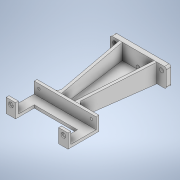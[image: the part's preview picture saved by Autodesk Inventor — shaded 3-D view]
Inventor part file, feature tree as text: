
AUTODESK INVENTOR PART (.ipt)
format: ipt  version: 2022 (Build 260153000, 153)  size: 266,240 bytes
history: native  units: mm
features: sketch x13, extrude x10, plane x1, loft x1, fillet x1, chamfer x1, other x1
ambient origin geometry x8: Origin, YZ Plane, XZ Plane, XY Plane, X Axis, Y Axis, Z Axis, Center Point
bodies: Solid1 (feature_tree)
feature tree (28):
  extrude  "Extrusion1"  Depth=3.0mm
  sketch  "Sketch2"  dims[d16=66.05mm d18=15.0mm]
  plane  "Work Plane1"
  loft  "Loft1"
  extrude  "Extrusion2"  Depth=3.0mm
  extrude  "Extrusion3"  Depth=3.0mm TaperAngle=0.0deg
  extrude  "Extrusion4"  Depth=7.5mm
  extrude  "Extrusion5"  Depth=56.05mm
  extrude  "Extrusion8"  Depth=2.5mm
  extrude  "Extrusion9"  TaperAngle=0.0deg  [1 undecoded]
  extrude  "Extrusion10"  Depth=5.0mm
  extrude  "Extrusion13"  Depth=5.0mm
  fillet  "Fillet1"  Radius=5.0mm
  chamfer  "Chamfer1"  Distance=1.0mm
  extrude  "Extrusion15"  Depth=20.0mm
  sketch  "Sketch1"  dims[d2=5.0mm d3=0.0mm d6=3.0mm d11=80.0mm]
  sketch  "Sketch3"  dims[d19=3.0mm d20=0.0mm d22=3.0mm]
  sketch  "Sketch4"  dims[d23=27.0mm d24=0.0mm d25=3.0mm d26=0.0mm]
  sketch  "Sketch5"  dims[d27=7.5mm d28=7.5mm]
  sketch  "Sketch6"  dims[d29=56.05mm d30=28.025mm]
  sketch  "Sketch7"  dims[d31=2.5mm d32=2.5mm]
  sketch  "Sketch10"  dims[d33=35.0mm d34=0.0mm d57=0.0mm d58=90.0deg]
  sketch  "Sketch11"  dims[d61=5.0mm d62=5.0mm]
  other  "Edges1"
  sketch  "Sketch12"  dims[d63=1.0mm d64=0.0mm d65=5.0mm d66=5.0mm d67=1.0mm d68=0.0mm]
  sketch  "Sketch15"  dims[d69=20.0mm d70=40.0mm]
  sketch  "Sketch16"  dims[d71=20.0mm]
  sketch  "Sketch17"  dims[d72=15.0mm d73=10.0mm d74=0.0mm d75=90.0deg d76=0.0mm d78=13.025mm d79=10.0mm d80=10.0mm d81=10.0mm d82=15.0mm d83=0.0mm d97=45.0deg d105=45.0deg d107=3.0mm d108=3.0mm d109=3.0mm d110=3.0mm d112=3.0mm d113=3.0mm d114=3.0mm d115=3.0mm d119=10.0mm d120=10.0mm d121=5.0mm d122=0.0mm d123=5.0mm d124=5.0mm d125=4.4mm d126=4.4mm d127=5.0mm d128=5.0mm d129=5.0mm d130=4.4mm d131=6.0mm d132=0.0mm d133=2.0mm d134=30.0mm d135=3.0mm d136=2.0mm d137=45.0deg d138=3.0mm d139=3.0mm d140=17.0mm d141=0.0mm]
note: 1 required parameter value undecoded (feature->parameter linkage not recoverable at this tier; creation-order binding heuristic only, values carry confidence <= 0.55)
